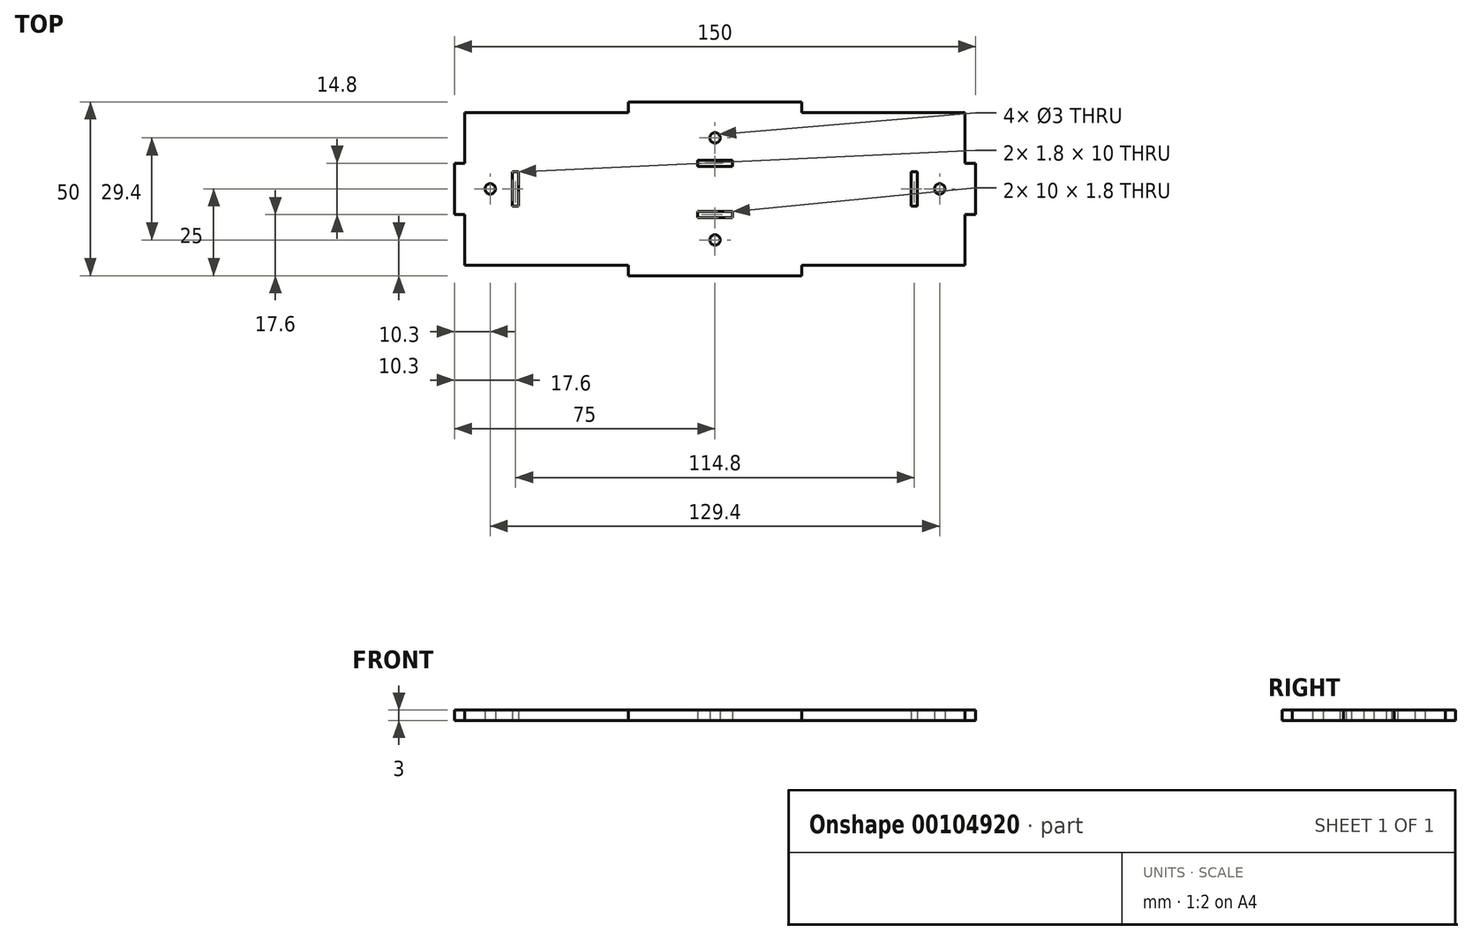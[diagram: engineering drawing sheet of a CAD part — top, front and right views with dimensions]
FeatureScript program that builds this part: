
annotation { "Feature Type Name" : "Feature", "Feature Type Description" : "" }
export const myFeature = defineFeature(function(context is Context, id is Id, definition is map)
    precondition{}
    {
        {
            var Q0;
            Q0=qCreatedBy(makeId("Top.planeOp"),FACE);
            var sketch = newSketch(context, id + "F0", { "sketchPlane" : qUnion([Q0])});
            skLineSegment(sketch, "E0.bottom", {"start": v(-72, 22) * mm, "end": v(-25, 22) * mm});
            skLineSegment(sketch, "E0.top", {"start": v(-72, -22) * mm, "end": v(-25, -22) * mm});
            skLineSegment(sketch, "E0.left", {"start": v(-72, 22) * mm, "end": v(-72, 7.33) * mm});
            skLineSegment(sketch, "E0.right", {"start": v(72, 22) * mm, "end": v(72, 7.33) * mm});
            skLineSegment(sketch, "E1.bottom", {"start": v(-72, 7.33) * mm, "end": v(-75, 7.33) * mm});
            skLineSegment(sketch, "E1.top", {"start": v(-72, -7.33) * mm, "end": v(-75, -7.33) * mm});
            skLineSegment(sketch, "E1.right", {"start": v(-75, 7.33) * mm, "end": v(-75, -7.33) * mm});
            skLineSegment(sketch, "E2.top", {"start": v(-25, 25) * mm, "end": v(25, 25) * mm});
            skLineSegment(sketch, "E2.left", {"start": v(-25, 22) * mm, "end": v(-25, 25) * mm});
            skLineSegment(sketch, "E2.right", {"start": v(25, 22) * mm, "end": v(25, 25) * mm});
            skLineSegment(sketch, "E3.bottom", {"start": v(72, 7.33) * mm, "end": v(75, 7.33) * mm});
            skLineSegment(sketch, "E3.top", {"start": v(72, -7.33) * mm, "end": v(75, -7.33) * mm});
            skLineSegment(sketch, "E3.right", {"start": v(75, 7.33) * mm, "end": v(75, -7.33) * mm});
            skLineSegment(sketch, "E4.top", {"start": v(25, -25) * mm, "end": v(-25, -25) * mm});
            skLineSegment(sketch, "E4.left", {"start": v(25, -22) * mm, "end": v(25, -25) * mm});
            skLineSegment(sketch, "E4.right", {"start": v(-25, -22) * mm, "end": v(-25, -25) * mm});
            skLineSegment(sketch, "E5.trimOffspring", {"start": v(25, 22) * mm, "end": v(72, 22) * mm});
            skLineSegment(sketch, "E6.trimOffspring", {"start": v(25, -22) * mm, "end": v(72, -22) * mm});
            skLineSegment(sketch, "E7.trimOffspring", {"start": v(-72, -7.33) * mm, "end": v(-72, -22) * mm});
            skLineSegment(sketch, "E8.trimOffspring", {"start": v(72, -7.33) * mm, "end": v(72, -22) * mm});
            skLineSegment(sketch, "E9", {"start": v(-75, 25) * mm, "end": v(-25, 25) * mm, "construction": true});
            skLineSegment(sketch, "E10", {"start": v(25, 25) * mm, "end": v(75, 25) * mm, "construction": true});
            skCircle(sketch, "E11", {"center": v(-64.7, 0) * mm, "radius": 1.5 * mm});
            skLineSegment(sketch, "E12.bottom", {"start": v(-58.3, 5) * mm, "end": v(-56.5, 5) * mm});
            skLineSegment(sketch, "E12.top", {"start": v(-58.3, -5) * mm, "end": v(-56.5, -5) * mm});
            skLineSegment(sketch, "E12.left", {"start": v(-58.3, 5) * mm, "end": v(-58.3, -5) * mm});
            skLineSegment(sketch, "E12.right", {"start": v(-56.5, 5) * mm, "end": v(-56.5, -5) * mm});
            skLineSegment(sketch, "E13.MirrorCS", {"start": v(58.3, 5) * mm, "end": v(56.5, 5) * mm});
            skLineSegment(sketch, "E14.MirrorCS", {"start": v(58.3, -5) * mm, "end": v(56.5, -5) * mm});
            skLineSegment(sketch, "E15.MirrorCS", {"start": v(56.5, 5) * mm, "end": v(56.5, -5) * mm});
            skLineSegment(sketch, "E16.MirrorCS", {"start": v(58.3, 5) * mm, "end": v(58.3, -5) * mm});
            skCircle(sketch, "E17", {"center": v(0, 14.7) * mm, "radius": 1.5 * mm});
            skLineSegment(sketch, "E18.bottom", {"start": v(5, 8.3) * mm, "end": v(-5, 8.3) * mm});
            skLineSegment(sketch, "E18.top", {"start": v(5, 6.5) * mm, "end": v(-5, 6.5) * mm});
            skLineSegment(sketch, "E18.left", {"start": v(5, 8.3) * mm, "end": v(5, 6.5) * mm});
            skLineSegment(sketch, "E18.right", {"start": v(-5, 8.3) * mm, "end": v(-5, 6.5) * mm});
            skLineSegment(sketch, "E19.MirrorCS", {"start": v(-5, -8.3) * mm, "end": v(-5, -6.5) * mm});
            skLineSegment(sketch, "E20.MirrorCS", {"start": v(5, -8.3) * mm, "end": v(5, -6.5) * mm});
            skCircle(sketch, "E21.MirrorC", {"center": v(0, -14.7) * mm, "radius": 1.5 * mm});
            skLineSegment(sketch, "E22.MirrorCS", {"start": v(5, -6.5) * mm, "end": v(-5, -6.5) * mm});
            skLineSegment(sketch, "E23.MirrorCS", {"start": v(5, -8.3) * mm, "end": v(-5, -8.3) * mm});
            skCircle(sketch, "E24.MirrorC", {"center": v(64.7, 0) * mm, "radius": 1.5 * mm});
            skSolve(sketch);
        }
        {
            var Q0;
            Q0=qSketchRegion(id+"F0",true);
            extrude(context, id + "F1", {"entities" : qUnion([Q0]), "depth" : 3 * mm});
        }
    });
